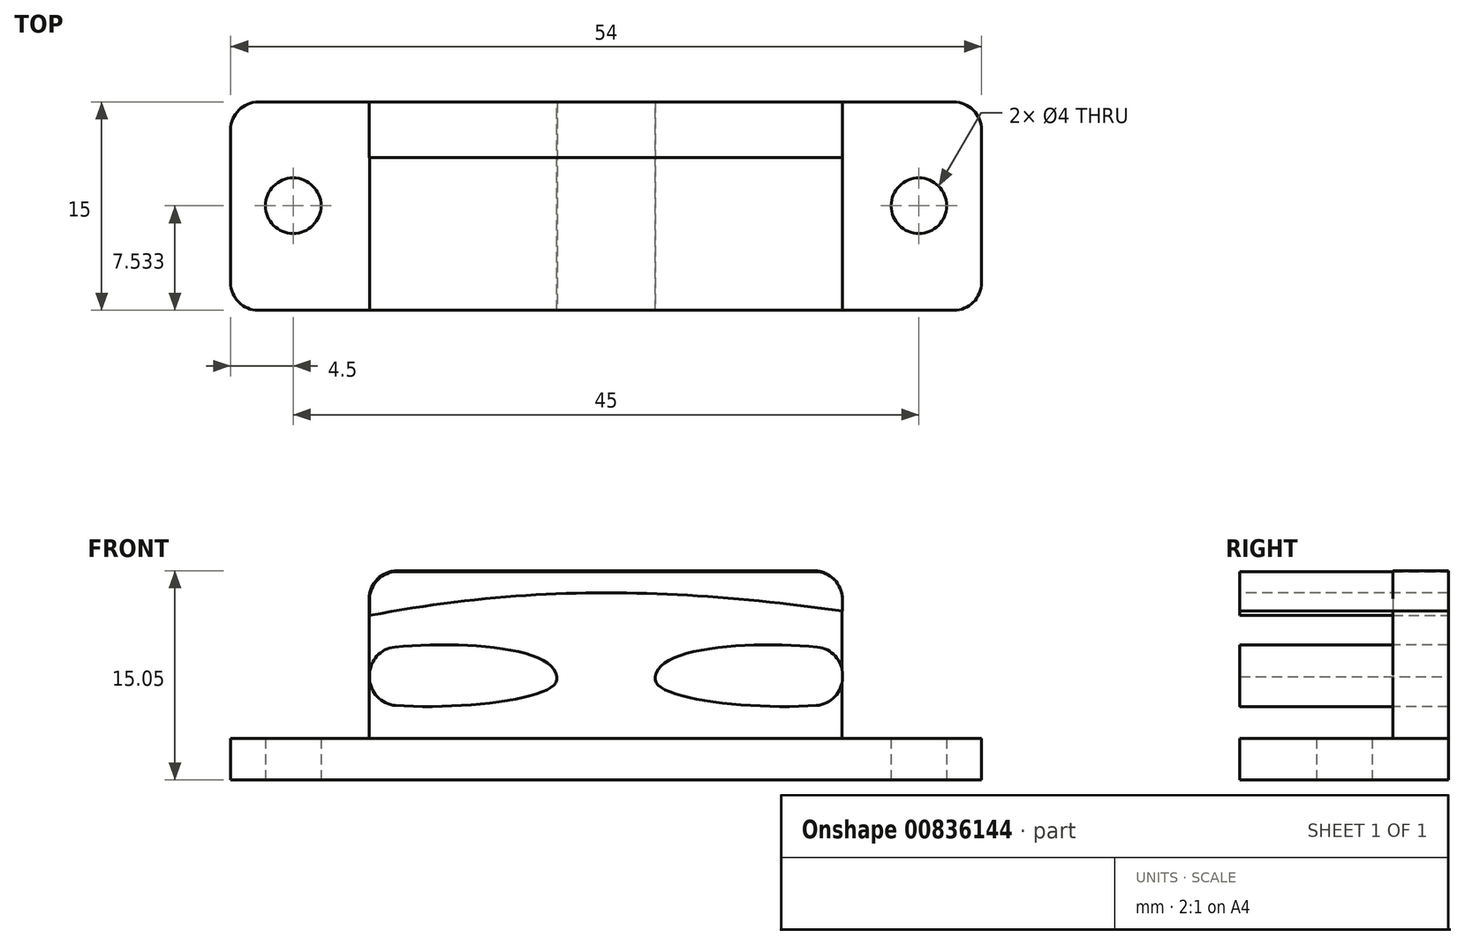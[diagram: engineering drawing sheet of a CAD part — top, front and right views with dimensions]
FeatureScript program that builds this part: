
annotation { "Feature Type Name" : "Feature", "Feature Type Description" : "" }
export const myFeature = defineFeature(function(context is Context, id is Id, definition is map)
    precondition{}
    {
        {
            var Q0;
            Q0=qCreatedBy(makeId("Top.planeOp"),FACE);
            var sketch = newSketch(context, id + "F0", { "sketchPlane" : qUnion([Q0])});
            skLineSegment(sketch, "E0.bottom", {"start": v(27, -7.5) * mm, "end": v(-27, -7.5) * mm});
            skLineSegment(sketch, "E0.top", {"start": v(27, 7.5) * mm, "end": v(-27, 7.5) * mm});
            skLineSegment(sketch, "E0.left", {"start": v(27, -7.5) * mm, "end": v(27, 7.5) * mm});
            skLineSegment(sketch, "E0.right", {"start": v(-27, -7.5) * mm, "end": v(-27, 7.5) * mm});
            skPoint(sketch, "E0.middle", {"position": v(0, 0) * mm});
            skLineSegment(sketch, "E1.left", {"start": v(22.5, -0.03) * mm, "end": v(22.5, 0.03) * mm});
            skLineSegment(sketch, "E1.right", {"start": v(-22.5, -0.03) * mm, "end": v(-22.5, 0.03) * mm});
            skCircle(sketch, "E2", {"center": v(-22.5, 0.03) * mm, "radius": 2 * mm});
            skCircle(sketch, "E3", {"center": v(22.5, 0.03) * mm, "radius": 2 * mm});
            skSolve(sketch);
        }
        {
            var Q0;
            Q0 = qSketchRegion(id + "F0", true);
            extrude(context, id + "F1", {"entities" : qUnion([Q0]), "depth" : 3 * mm, "offsetDistance" : 25 * mm});
        }
        {
            var Q0;
            Q0=makeQuery(id+"F1.opExtrude","SWEPT_FACE",FACE,{"disambiguationData":[OSD([sQuery(id+"F0.wireOp",EDGE,"E0.top")])]});
            var sketch = newSketch(context, id + "F2", { "sketchPlane" : qUnion([Q0])});
            skPoint(sketch, "E4.middle", {"position": v(0, 0) * mm});
            skLineSegment(sketch, "E5.bottom", {"start": v(-17, 15) * mm, "end": v(17, 15) * mm});
            skLineSegment(sketch, "E5.top", {"start": v(-17, 0) * mm, "end": v(17, 0) * mm});
            skLineSegment(sketch, "E5.left", {"start": v(-17, 15) * mm, "end": v(-17, 0) * mm});
            skLineSegment(sketch, "E5.right", {"start": v(17, 15) * mm, "end": v(17, 0) * mm});
            skLineSegment(sketch, "E6", {"start": v(0, 0) * mm, "end": v(0, 15) * mm});
            skFitSpline(sketch, "E7", {"points": [v(-17, 9.32) * mm, v(-3.55, 7.42) * mm], "startDerivative": vector(12.77, 2.27) * mm, "endDerivative": vector(0.71, -7.54) * mm});
            skFitSpline(sketch, "E8", {"points": [v(-17, 5.58) * mm, v(-3.55, 7.42) * mm], "startDerivative": vector(12.63, -2.27) * mm, "endDerivative": vector(-1.7, 5.55) * mm});
            skFitSpline(sketch, "E9.MirrorCS", {"points": [v(17, 9.32) * mm, v(3.55, 7.42) * mm], "startDerivative": vector(-12.77, 2.27) * mm, "endDerivative": vector(-0.71, -7.54) * mm});
            skFitSpline(sketch, "E10.MirrorCS", {"points": [v(17, 5.58) * mm, v(3.55, 7.42) * mm], "startDerivative": vector(-12.63, -2.27) * mm, "endDerivative": vector(1.7, 5.55) * mm});
            skLineSegment(sketch, "E11", {"start": v(-17, 9.32) * mm, "end": v(-17, 5.58) * mm});
            skLineSegment(sketch, "E12", {"start": v(17, 9.32) * mm, "end": v(17, 5.58) * mm});
            skFitSpline(sketch, "E13", {"points": [v(-17, 12.16) * mm, v(17, 11.84) * mm], "startDerivative": vector(34.55, 4.78) * mm, "endDerivative": vector(36.13, -6.93) * mm});
            skSolve(sketch);
        }
        {
            var Q0;
            Q0=makeQuery(id+"F2.imprint","IMPRINT",FACE,{"disambiguationData":[TD([[makeQuery(id+"F2.imprint","IMPRINT",EDGE,{"derivedFrom":sQuery(id+"F2.wireOp",EDGE,"E7")}),-1.0]])]});
            var Q1;
            Q1=makeQuery(id+"F2.imprint","IMPRINT",FACE,{"disambiguationData":[TD([[makeQuery(id+"F2.imprint","IMPRINT",EDGE,{"derivedFrom":sQuery(id+"F2.wireOp",EDGE,"E9.MirrorCS")}),1.0]])]});
            var Q2;
            {var subQ0=sQuery(id+"F2.wireOp",EDGE,"E5.right");var subQ1=sQuery(id+"F2.wireOp",EDGE,"E5.bottom");var subQ2=makeQuery(id+"F2.imprint","INTERSECT",VERTEX,{"derivedFrom":[subQ1,subQ0]});Q2=makeQuery(id+"F2.imprint","IMPRINT",FACE,{"disambiguationData":[TD([[makeQuery(id+"F2.imprint","IMPRINT",EDGE,{"disambiguationData":[TD([[subQ2,1.0]])],"derivedFrom":subQ1}),-1.0]])]});}
            var Q3;
            {var subQ0=sQuery(id+"F2.wireOp",EDGE,"E5.left");var subQ1=sQuery(id+"F2.wireOp",EDGE,"E5.bottom");var subQ2=makeQuery(id+"F2.imprint","INTERSECT",VERTEX,{"derivedFrom":[subQ1,subQ0]});Q3=makeQuery(id+"F2.imprint","IMPRINT",FACE,{"disambiguationData":[TD([[makeQuery(id+"F2.imprint","IMPRINT",EDGE,{"disambiguationData":[TD([[subQ2,-1.0]])],"derivedFrom":subQ1}),-1.0]])]});}
            extrude(context, id + "F3", {"entities" : qUnion([Q0, Q1, Q2, Q3]), "oppositeDirection" : true, "depth" : 15 * mm, "offsetDistance" : 25 * mm});
        }
        {
            var Q0;
            Q0=makeQuery(id+"F1.opExtrude","SWEPT_FACE",FACE,{"disambiguationData":[OSD([sQuery(id+"F0.wireOp",EDGE,"E0.top")])]});
            var sketch = newSketch(context, id + "F4", { "sketchPlane" : qUnion([Q0])});
            skLineSegment(sketch, "E14.bottom", {"start": v(-16.96, 15.05) * mm, "end": v(17.03, 15.05) * mm});
            skLineSegment(sketch, "E14.top", {"start": v(-16.96, 0) * mm, "end": v(17.03, 0) * mm});
            skLineSegment(sketch, "E14.left", {"start": v(-16.96, 15.05) * mm, "end": v(-16.96, 0) * mm});
            skLineSegment(sketch, "E14.right", {"start": v(17.03, 15.05) * mm, "end": v(17.03, 0) * mm});
            skSolve(sketch);
        }
        {
            var Q0;
            {var subQ0=sQuery(id+"F4.wireOp",EDGE,"E14.bottom");Q0=makeQuery(id+"F4.imprint","IMPRINT",FACE,{"disambiguationData":[TD([[makeQuery(id+"F4.imprint","IMPRINT",EDGE,{"derivedFrom":subQ0}),-1.0]])]});}
            extrude(context, id + "F5", {"entities" : qUnion([Q0]), "oppositeDirection" : true, "depth" : 4 * mm, "offsetDistance" : 25 * mm});
        }
        {
            var Q0;
            Q0=makeQuery(id+"F1.opExtrude","SWEPT_EDGE",EDGE,{"disambiguationData":[OSD([sQuery(id+"F0.wireOp",EDGE,"E0.top"),sQuery(id+"F0.wireOp",EDGE,"E0.right")])]});
            var Q1;
            Q1=makeQuery(id+"F1.opExtrude","SWEPT_EDGE",EDGE,{"disambiguationData":[OSD([sQuery(id+"F0.wireOp",EDGE,"E0.bottom"),sQuery(id+"F0.wireOp",EDGE,"E0.right")])]});
            var Q2;
            Q2=makeQuery(id+"F1.opExtrude","SWEPT_EDGE",EDGE,{"disambiguationData":[OSD([sQuery(id+"F0.wireOp",EDGE,"E0.bottom"),sQuery(id+"F0.wireOp",EDGE,"E0.left")])]});
            var Q3;
            Q3=makeQuery(id+"F1.opExtrude","SWEPT_EDGE",EDGE,{"disambiguationData":[OSD([sQuery(id+"F0.wireOp",EDGE,"E0.top"),sQuery(id+"F0.wireOp",EDGE,"E0.left")])]});
            var Q4;
            Q4=makeQuery(id+"F3.opExtrude","SWEPT_EDGE",EDGE,{"disambiguationData":[OSD([sQuery(id+"F2.wireOp",EDGE,"E5.bottom"),sQuery(id+"F2.wireOp",EDGE,"E5.right")])]});
            var Q5;
            Q5=makeQuery(id+"F3.opExtrude","SWEPT_EDGE",EDGE,{"disambiguationData":[OSD([sQuery(id+"F2.wireOp",EDGE,"E5.bottom"),sQuery(id+"F2.wireOp",EDGE,"E5.left")])]});
            var Q6;
            Q6=makeQuery(id+"F5.opExtrude","SWEPT_EDGE",EDGE,{"disambiguationData":[OSD([sQuery(id+"F4.wireOp",EDGE,"E14.bottom"),sQuery(id+"F4.wireOp",EDGE,"E14.right")])]});
            var Q7;
            Q7=makeQuery(id+"F5.opExtrude","SWEPT_EDGE",EDGE,{"disambiguationData":[OSD([sQuery(id+"F4.wireOp",EDGE,"E14.bottom"),sQuery(id+"F4.wireOp",EDGE,"E14.left")])]});
            var Q8;
            Q8=makeQuery(id+"F3.opExtrude","SWEPT_EDGE",EDGE,{"disambiguationData":[OSD([sQuery(id+"F2.wireOp",EDGE,"E5.right"),sQuery(id+"F2.wireOp",EDGE,"E9.MirrorCS"),sQuery(id+"F2.wireOp",EDGE,"E12")])]});
            var Q9;
            Q9=makeQuery(id+"F3.opExtrude","SWEPT_EDGE",EDGE,{"disambiguationData":[OSD([sQuery(id+"F2.wireOp",EDGE,"E5.right"),sQuery(id+"F2.wireOp",EDGE,"E10.MirrorCS"),sQuery(id+"F2.wireOp",EDGE,"E12")])]});
            var Q10;
            Q10=makeQuery(id+"F3.opExtrude","SWEPT_EDGE",EDGE,{"disambiguationData":[OSD([sQuery(id+"F2.wireOp",EDGE,"E5.left"),sQuery(id+"F2.wireOp",EDGE,"E7"),sQuery(id+"F2.wireOp",EDGE,"E11")])]});
            var Q11;
            Q11=makeQuery(id+"F3.opExtrude","SWEPT_EDGE",EDGE,{"disambiguationData":[OSD([sQuery(id+"F2.wireOp",EDGE,"E5.left"),sQuery(id+"F2.wireOp",EDGE,"E8"),sQuery(id+"F2.wireOp",EDGE,"E11")])]});
            fillet(context, id + "F6", {"entities" : qUnion([Q0, Q1, Q2, Q3, Q4, Q5, Q6, Q7, Q8, Q9, Q10, Q11]), "radius" : 2 * mm, "tangentPropagation" : true, "allowEdgeOverflow" : false});
        }
    });
